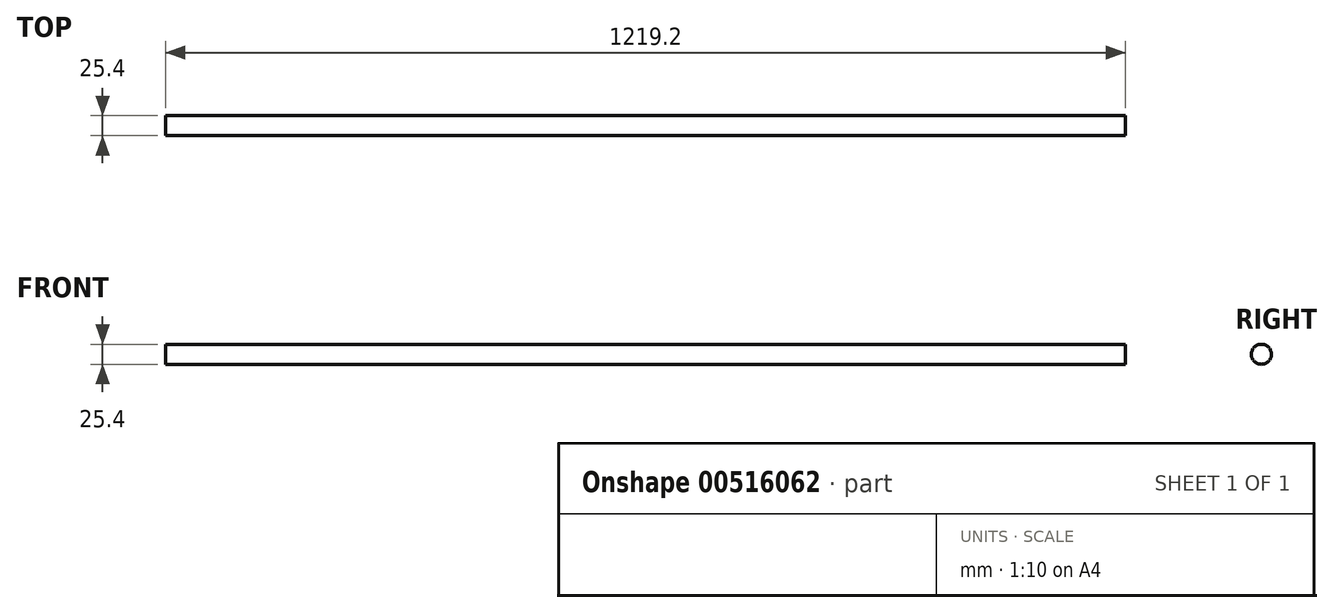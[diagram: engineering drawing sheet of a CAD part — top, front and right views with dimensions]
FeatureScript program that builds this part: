
annotation { "Feature Type Name" : "Feature", "Feature Type Description" : "" }
export const myFeature = defineFeature(function(context is Context, id is Id, definition is map)
    precondition{}
    {
        {
            var Q0;
            Q0=qCreatedBy(makeId("Right.planeOp"),FACE);
            var sketch = newSketch(context, id + "F0", { "sketchPlane" : qUnion([Q0])});
            skCircle(sketch, "E0", {"center": v(0, 0) * mm, "radius": 12.7 * mm});
            skSolve(sketch);
        }
        {
            var Q0;
            Q0=makeQuery(id+"F0.imprint","IMPRINT",FACE,{"disambiguationData":[TD([[makeQuery(id+"F0.imprint","IMPRINT",EDGE,{"derivedFrom":sQuery(id+"F0.wireOp",EDGE,"E0")}),1.0]])]});
            extrude(context, id + "F1", {"entities" : qUnion([Q0]), "depth" : 1219.2 * mm, "offsetDistance" : 25.4 * mm});
        }
    });
